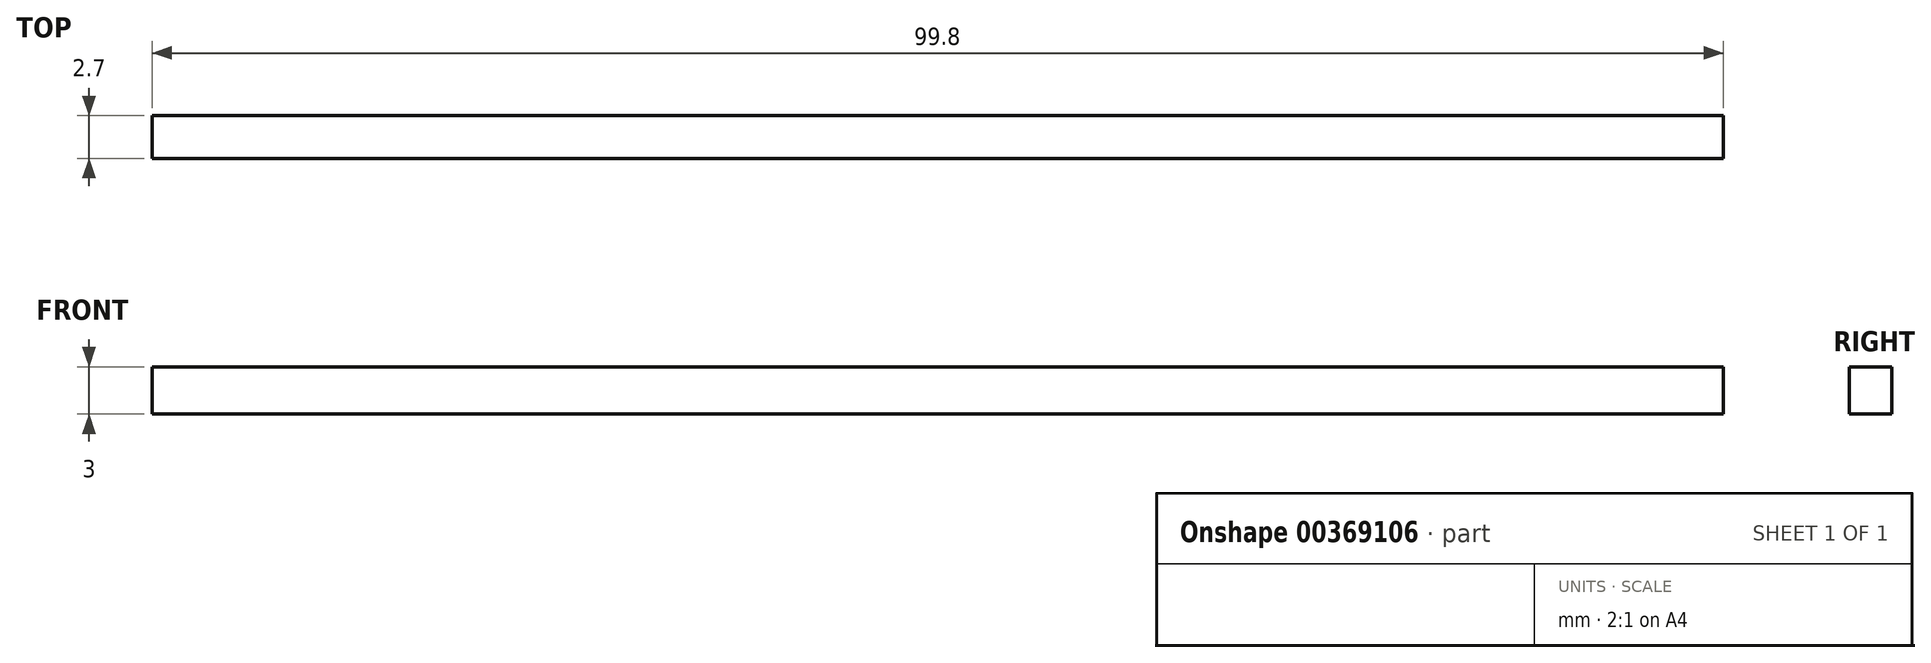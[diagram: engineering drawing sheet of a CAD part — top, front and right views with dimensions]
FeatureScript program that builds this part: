
annotation { "Feature Type Name" : "Feature", "Feature Type Description" : "" }
export const myFeature = defineFeature(function(context is Context, id is Id, definition is map)
    precondition{}
    {
        {
            var Q0;
            Q0=qCreatedBy(makeId("Top.planeOp"),FACE);
            var sketch = newSketch(context, id + "F0", { "sketchPlane" : qUnion([Q0])});
            skLineSegment(sketch, "E0.bottom", {"start": v(49.9, -1.35) * mm, "end": v(-49.9, -1.35) * mm});
            skLineSegment(sketch, "E0.top", {"start": v(49.9, 1.35) * mm, "end": v(-49.9, 1.35) * mm});
            skLineSegment(sketch, "E0.left", {"start": v(49.9, -1.35) * mm, "end": v(49.9, 1.35) * mm});
            skLineSegment(sketch, "E0.right", {"start": v(-49.9, -1.35) * mm, "end": v(-49.9, 1.35) * mm});
            skPoint(sketch, "E0.middle", {"position": v(0, 0) * mm});
            skSolve(sketch);
        }
        {
            var Q0;
            Q0 = qSketchRegion(id + "F0", true);
            extrude(context, id + "F1", {"entities" : qUnion([Q0]), "depth" : 3 * mm});
        }
    });
